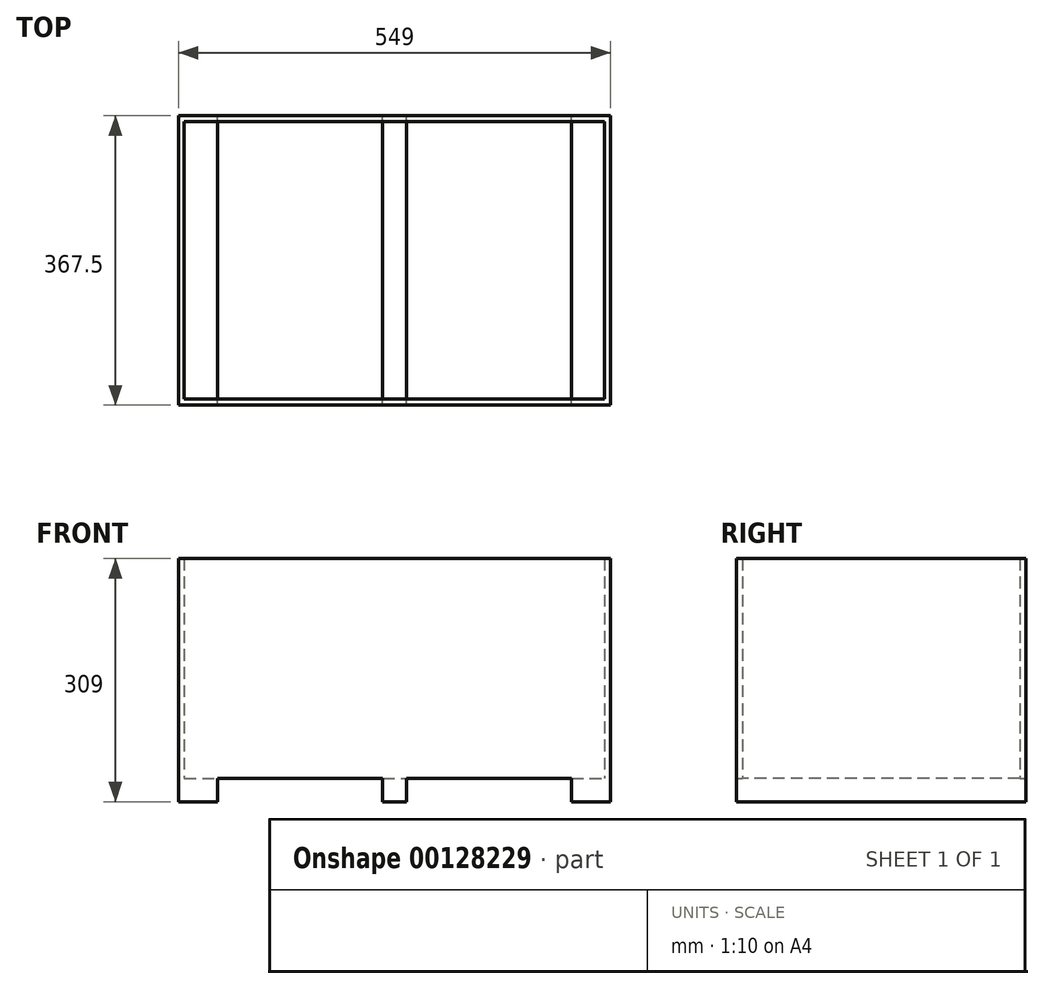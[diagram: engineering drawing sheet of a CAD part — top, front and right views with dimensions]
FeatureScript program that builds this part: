
annotation { "Feature Type Name" : "Feature", "Feature Type Description" : "" }
export const myFeature = defineFeature(function(context is Context, id is Id, definition is map)
    precondition{}
    {
        {
            var Q0;
            Q0=qCreatedBy(makeId("Top.planeOp"),FACE);
            var sketch = newSketch(context, id + "F0", { "sketchPlane" : qUnion([Q0])});
            skLineSegment(sketch, "E0.bottom", {"start": v(-272.65, 169.58) * mm, "end": v(276.35, 169.58) * mm});
            skLineSegment(sketch, "E0.top", {"start": v(-272.65, -197.92) * mm, "end": v(276.35, -197.92) * mm});
            skLineSegment(sketch, "E0.left", {"start": v(-272.65, 169.58) * mm, "end": v(-272.65, -197.92) * mm});
            skLineSegment(sketch, "E0.right", {"start": v(276.35, 169.58) * mm, "end": v(276.35, -197.92) * mm});
            skSolve(sketch);
        }
        {
            var Q0;
            Q0 = qSketchRegion(id + "F0", true);
            extrude(context, id + "F1", {"entities" : qUnion([Q0]), "depth" : 279 * mm});
        }
        {
            var Q0;
            Q0=makeQuery(id+"F1.opExtrude","CAP_FACE",FACE,{"disambiguationData":[OSD([sQuery(id+"F0.wireOp",EDGE,"E0.bottom"),sQuery(id+"F0.wireOp",EDGE,"E0.top"),sQuery(id+"F0.wireOp",EDGE,"E0.left"),sQuery(id+"F0.wireOp",EDGE,"E0.right")])],"isStart":false});
            var Q1;
            Q1=makeQuery(id+"F1.opExtrude","CAP_FACE",FACE,{"disambiguationData":[OSD([sQuery(id+"F0.wireOp",EDGE,"E0.bottom"),sQuery(id+"F0.wireOp",EDGE,"E0.top"),sQuery(id+"F0.wireOp",EDGE,"E0.left"),sQuery(id+"F0.wireOp",EDGE,"E0.right")])],"isStart":true});
            shell(context, id + "F2", {"entities" : qUnion([Q0, Q1]), "thickness" : 7.5 * mm});
        }
        {
            var Q0;
            Q0=makeQuery(id+"F1.opExtrude","CAP_FACE",FACE,{"disambiguationData":[OSD([sQuery(id+"F0.wireOp",EDGE,"E0.bottom"),sQuery(id+"F0.wireOp",EDGE,"E0.top"),sQuery(id+"F0.wireOp",EDGE,"E0.left"),sQuery(id+"F0.wireOp",EDGE,"E0.right")])],"isStart":true});
            var sketch = newSketch(context, id + "F3", { "sketchPlane" : qUnion([Q0])});
            skLineSegment(sketch, "E1.bottom", {"start": v(-272.65, 197.92) * mm, "end": v(-223.15, 197.92) * mm});
            skLineSegment(sketch, "E1.top", {"start": v(-272.65, -169.58) * mm, "end": v(-223.15, -169.58) * mm});
            skLineSegment(sketch, "E1.left", {"start": v(-272.65, 197.92) * mm, "end": v(-272.65, -169.58) * mm});
            skLineSegment(sketch, "E1.right", {"start": v(-223.15, 197.92) * mm, "end": v(-223.15, -169.58) * mm});
            skLineSegment(sketch, "E2.bottom", {"start": v(-13.15, 197.92) * mm, "end": v(16.85, 197.92) * mm});
            skLineSegment(sketch, "E2.top", {"start": v(-13.15, -169.58) * mm, "end": v(16.85, -169.58) * mm});
            skLineSegment(sketch, "E2.left", {"start": v(-13.15, 197.92) * mm, "end": v(-13.15, -169.58) * mm});
            skLineSegment(sketch, "E2.right", {"start": v(16.85, 197.92) * mm, "end": v(16.85, -169.58) * mm});
            skLineSegment(sketch, "E3.bottom", {"start": v(276.35, 197.92) * mm, "end": v(226.85, 197.92) * mm});
            skLineSegment(sketch, "E3.top", {"start": v(276.35, -169.58) * mm, "end": v(226.85, -169.58) * mm});
            skLineSegment(sketch, "E3.left", {"start": v(276.35, 197.92) * mm, "end": v(276.35, -169.58) * mm});
            skLineSegment(sketch, "E3.right", {"start": v(226.85, 197.92) * mm, "end": v(226.85, -169.58) * mm});
            skSolve(sketch);
        }
        {
            var Q0;
            Q0 = qSketchRegion(id + "F3", true);
            extrude(context, id + "F4", {"entities" : qUnion([Q0]), "operationType" : NewBodyOperationType.ADD, "depth" : 30 * mm});
        }
    });
